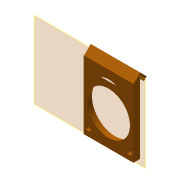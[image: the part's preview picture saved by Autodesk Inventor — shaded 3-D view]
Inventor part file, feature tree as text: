
AUTODESK INVENTOR PART (.ipt)
format: ipt  version: 2022 (Build 260153000, 153)  size: 165,888 bytes
history: native  units: mm
features: extrude x5, sketch x5, reference x3, other x3, projected_geometry x2, plane x1
ambient origin geometry x8: Origin, YZ Plane, XZ Plane, XY Plane, X Axis, Y Axis, Z Axis, Center Point
bodies: Volumenkörper1 (feature_tree)
feature tree (19):
  plane  "Arbeitsebene1"
  extrude  "Extrusion1"  Depth=27.5mm
  extrude  "Extrusion2"  Depth=25.7mm
  extrude  "Extrusion3"  Depth=5.0mm
  extrude  "Extrusion4"  Depth=5.0mm
  extrude  "Extrusion5"  Depth=10.0mm
  sketch  "Skizze1"  dims[d0=27.5mm d1=4.0mm]
  sketch  "Skizze2"  dims[d2=1.5mm d3=25.7mm]
  projected_geometry  "Projizierte Kontur1"
  reference  "Referenz2"
  sketch  "Skizze3"  dims[d4=3.3mm d5=0.0mm d6=5.0mm]
  projected_geometry  "Projizierte Kontur2"
  sketch  "Skizze4"  dims[d7=5.0mm d8=0.15mm]
  reference  "Referenz3"
  sketch  "Skizze5"  dims[d9=3.3mm d10=0.0mm d11=1.0mm d12=0.3mm d13=0.0mm d14=7.0mm d15=0.0mm d16=10.0mm d17=0.0mm d18=0.5mm d19=0.872665mm]
  reference  "Referenz4"
  other  "Assembly_Cube_Dichroic_Beamsplitter_multi_motorized_25x35_linearmotor_v3.iam"
  other  "30_Cube_Insert_Filter_Revolver_Filter_base_triple_linearmotor:1"
  other  "Assembly_Cube_Dichroic_Beamsplitter_multi_motorized_25x35_v3.iam"
